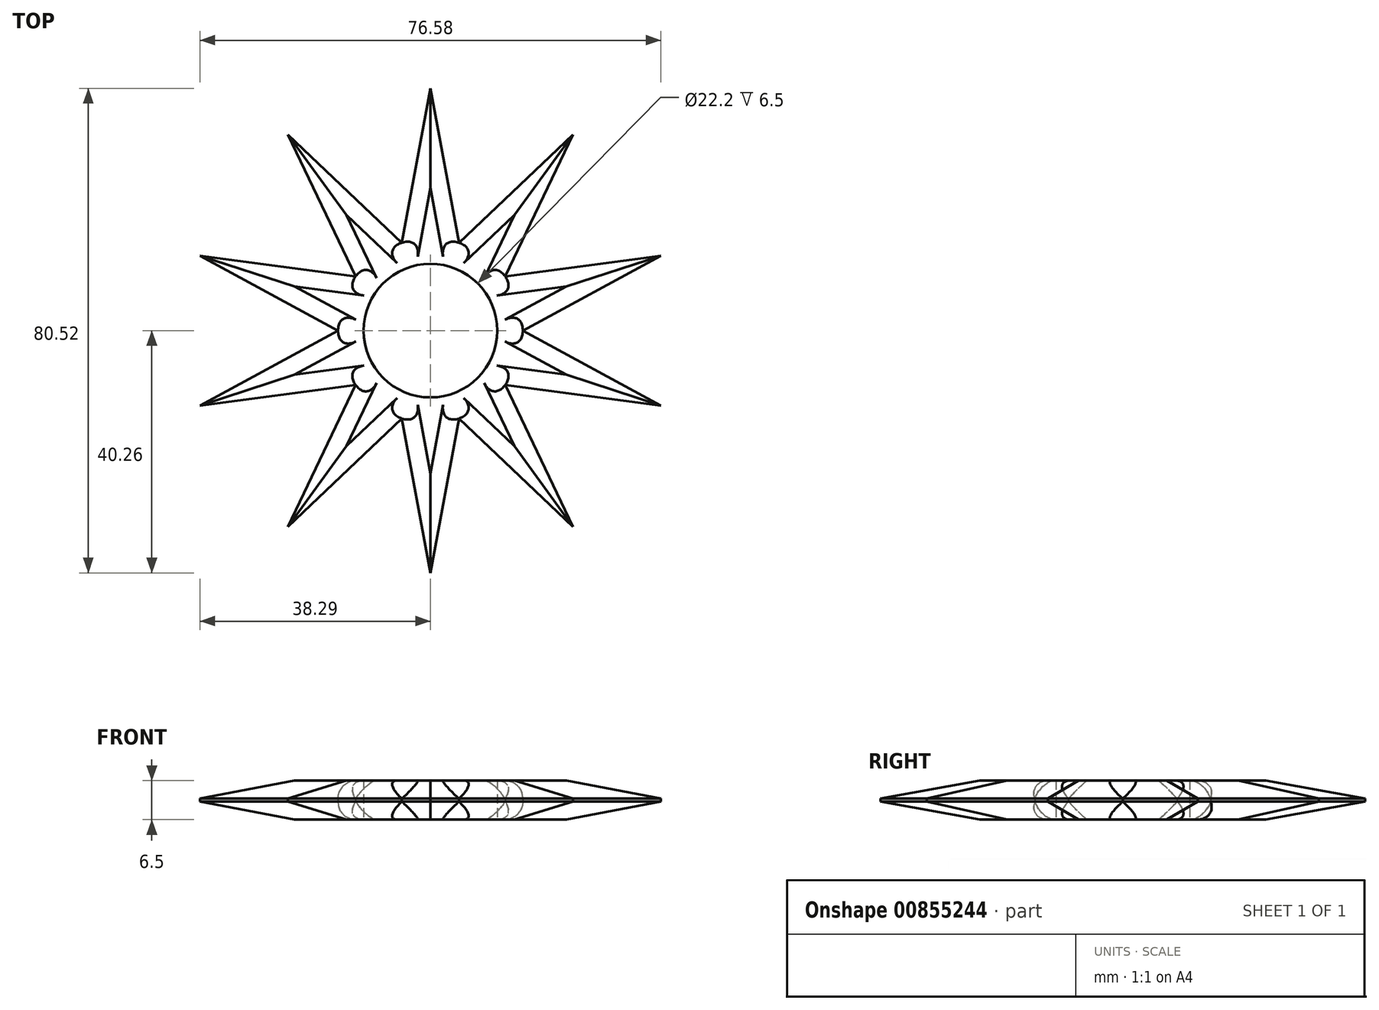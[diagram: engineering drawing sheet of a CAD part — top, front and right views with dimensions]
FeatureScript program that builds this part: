
annotation { "Feature Type Name" : "Feature", "Feature Type Description" : "" }
export const myFeature = defineFeature(function(context is Context, id is Id, definition is map)
    precondition{}
    {
        {
            var Q0;
            Q0=qCreatedBy(makeId("Top.planeOp"),FACE);
            var sketch = newSketch(context, id + "F0", { "sketchPlane" : qUnion([Q0])});
            skCircle(sketch, "E0", {"center": v(0, 0) * mm, "radius": 11.1 * mm});
            skArc(sketch, "E1", {"start": v(-4.74, 14.62) * mm, "mid": v(-4.75, 14.61) * mm, "end": v(-4.76, 14.61) * mm});
            skLineSegment(sketch, "E2", {"start": v(-4.74, 14.62) * mm, "end": v(0, 40.26) * mm});
            skLineSegment(sketch, "E3", {"start": v(0, 40.26) * mm, "end": v(4.74, 14.62) * mm});
            skLineSegment(sketch, "E4.1.0", {"start": v(-23.66, 32.57) * mm, "end": v(-4.76, 14.61) * mm});
            skLineSegment(sketch, "E4.1.1", {"start": v(-12.43, 9.04) * mm, "end": v(-23.66, 32.57) * mm});
            skLineSegment(sketch, "E4.2.0", {"start": v(-38.29, 12.44) * mm, "end": v(-12.43, 9.02) * mm});
            skLineSegment(sketch, "E4.2.1", {"start": v(-15.36, 0) * mm, "end": v(-38.29, 12.44) * mm});
            skLineSegment(sketch, "E4.3.0", {"start": v(-38.29, -12.44) * mm, "end": v(-15.36, 0) * mm});
            skLineSegment(sketch, "E4.3.1", {"start": v(-12.43, -9.02) * mm, "end": v(-38.29, -12.44) * mm});
            skLineSegment(sketch, "E4.4.0", {"start": v(-23.66, -32.57) * mm, "end": v(-12.43, -9.04) * mm});
            skLineSegment(sketch, "E4.4.1", {"start": v(-4.76, -14.61) * mm, "end": v(-23.66, -32.57) * mm});
            skLineSegment(sketch, "E4.5.0", {"start": v(0, -40.26) * mm, "end": v(-4.74, -14.62) * mm});
            skLineSegment(sketch, "E4.5.1", {"start": v(4.74, -14.62) * mm, "end": v(0, -40.26) * mm});
            skLineSegment(sketch, "E4.6.0", {"start": v(23.66, -32.57) * mm, "end": v(4.76, -14.61) * mm});
            skLineSegment(sketch, "E4.6.1", {"start": v(12.43, -9.04) * mm, "end": v(23.66, -32.57) * mm});
            skLineSegment(sketch, "E4.7.0", {"start": v(38.29, -12.44) * mm, "end": v(12.43, -9.02) * mm});
            skLineSegment(sketch, "E4.7.1", {"start": v(15.36, 0) * mm, "end": v(38.29, -12.44) * mm});
            skLineSegment(sketch, "E4.8.0", {"start": v(38.29, 12.44) * mm, "end": v(15.36, 0) * mm});
            skLineSegment(sketch, "E4.8.1", {"start": v(12.43, 9.02) * mm, "end": v(38.29, 12.44) * mm});
            skLineSegment(sketch, "E4.9.0", {"start": v(23.66, 32.57) * mm, "end": v(12.43, 9.04) * mm});
            skLineSegment(sketch, "E4.9.1", {"start": v(4.76, 14.61) * mm, "end": v(23.66, 32.57) * mm});
            skArc(sketch, "E5.trimOffspring", {"start": v(4.76, 14.61) * mm, "mid": v(4.75, 14.61) * mm, "end": v(4.74, 14.62) * mm});
            skArc(sketch, "E6.trimOffspring", {"start": v(12.43, 9.02) * mm, "mid": v(12.43, 9.03) * mm, "end": v(12.43, 9.04) * mm});
            skArc(sketch, "E7.trimOffspring", {"start": v(15.36, 0) * mm, "mid": v(15.36, 0) * mm, "end": v(15.36, 0) * mm});
            skArc(sketch, "E8.trimOffspring", {"start": v(12.43, -9.04) * mm, "mid": v(12.43, -9.03) * mm, "end": v(12.43, -9.02) * mm});
            skArc(sketch, "E9.trimOffspring", {"start": v(4.74, -14.62) * mm, "mid": v(4.75, -14.61) * mm, "end": v(4.76, -14.61) * mm});
            skArc(sketch, "E10.trimOffspring", {"start": v(-4.76, -14.61) * mm, "mid": v(-4.75, -14.61) * mm, "end": v(-4.74, -14.62) * mm});
            skArc(sketch, "E11.trimOffspring", {"start": v(-12.43, -9.02) * mm, "mid": v(-12.43, -9.03) * mm, "end": v(-12.43, -9.04) * mm});
            skArc(sketch, "E12.trimOffspring", {"start": v(-15.36, 0) * mm, "mid": v(-15.36, 0) * mm, "end": v(-15.36, 0) * mm});
            skArc(sketch, "E13.trimOffspring", {"start": v(-12.43, 9.04) * mm, "mid": v(-12.43, 9.03) * mm, "end": v(-12.43, 9.02) * mm});
            skSolve(sketch);
        }
        {
            var Q0;
            Q0=makeQuery(id+"F0.imprint","IMPRINT",FACE,{"disambiguationData":[TD([[makeQuery(id+"F0.imprint","IMPRINT",EDGE,{"derivedFrom":sQuery(id+"F0.wireOp",EDGE,"E0")}),-1.0]])]});
            extrude(context, id + "F1", {"entities" : qUnion([Q0]), "depth" : 6.5 * mm, "offsetDistance" : 25 * mm});
        }
        {
            var Q0;
            Q0=makeQuery(id+"F1.opExtrude","CAP_EDGE",EDGE,{"disambiguationData":[OSD([sQuery(id+"F0.wireOp",EDGE,"E4.3.0")])],"isStart":false});
            var Q1;
            Q1=makeQuery(id+"F1.opExtrude","CAP_EDGE",EDGE,{"disambiguationData":[OSD([sQuery(id+"F0.wireOp",EDGE,"E4.2.1")])],"isStart":false});
            var Q2;
            Q2=makeQuery(id+"F1.opExtrude","CAP_EDGE",EDGE,{"disambiguationData":[OSD([sQuery(id+"F0.wireOp",EDGE,"E4.2.0")])],"isStart":false});
            var Q3;
            Q3=makeQuery(id+"F1.opExtrude","CAP_EDGE",EDGE,{"disambiguationData":[OSD([sQuery(id+"F0.wireOp",EDGE,"E4.1.1")])],"isStart":false});
            var Q4;
            Q4=makeQuery(id+"F1.opExtrude","CAP_EDGE",EDGE,{"disambiguationData":[OSD([sQuery(id+"F0.wireOp",EDGE,"E4.1.0")])],"isStart":false});
            var Q5;
            Q5=makeQuery(id+"F1.opExtrude","CAP_EDGE",EDGE,{"disambiguationData":[OSD([sQuery(id+"F0.wireOp",EDGE,"E2")])],"isStart":false});
            var Q6;
            Q6=makeQuery(id+"F1.opExtrude","CAP_EDGE",EDGE,{"disambiguationData":[OSD([sQuery(id+"F0.wireOp",EDGE,"E3")])],"isStart":false});
            var Q7;
            Q7=makeQuery(id+"F1.opExtrude","CAP_EDGE",EDGE,{"disambiguationData":[OSD([sQuery(id+"F0.wireOp",EDGE,"E4.9.1")])],"isStart":false});
            var Q8;
            Q8=makeQuery(id+"F1.opExtrude","CAP_EDGE",EDGE,{"disambiguationData":[OSD([sQuery(id+"F0.wireOp",EDGE,"E4.9.0")])],"isStart":false});
            var Q9;
            Q9=makeQuery(id+"F1.opExtrude","CAP_EDGE",EDGE,{"disambiguationData":[OSD([sQuery(id+"F0.wireOp",EDGE,"E4.8.1")])],"isStart":false});
            var Q10;
            Q10=makeQuery(id+"F1.opExtrude","CAP_EDGE",EDGE,{"disambiguationData":[OSD([sQuery(id+"F0.wireOp",EDGE,"E4.8.0")])],"isStart":false});
            var Q11;
            Q11=makeQuery(id+"F1.opExtrude","CAP_EDGE",EDGE,{"disambiguationData":[OSD([sQuery(id+"F0.wireOp",EDGE,"E4.7.1")])],"isStart":false});
            var Q12;
            Q12=makeQuery(id+"F1.opExtrude","CAP_EDGE",EDGE,{"disambiguationData":[OSD([sQuery(id+"F0.wireOp",EDGE,"E4.7.0")])],"isStart":false});
            var Q13;
            Q13=makeQuery(id+"F1.opExtrude","CAP_EDGE",EDGE,{"disambiguationData":[OSD([sQuery(id+"F0.wireOp",EDGE,"E4.6.1")])],"isStart":false});
            var Q14;
            Q14=makeQuery(id+"F1.opExtrude","CAP_EDGE",EDGE,{"disambiguationData":[OSD([sQuery(id+"F0.wireOp",EDGE,"E4.6.0")])],"isStart":false});
            var Q15;
            Q15=makeQuery(id+"F1.opExtrude","CAP_EDGE",EDGE,{"disambiguationData":[OSD([sQuery(id+"F0.wireOp",EDGE,"E4.5.1")])],"isStart":false});
            var Q16;
            Q16=makeQuery(id+"F1.opExtrude","CAP_EDGE",EDGE,{"disambiguationData":[OSD([sQuery(id+"F0.wireOp",EDGE,"E4.4.0")])],"isStart":false});
            var Q17;
            Q17=makeQuery(id+"F1.opExtrude","CAP_EDGE",EDGE,{"disambiguationData":[OSD([sQuery(id+"F0.wireOp",EDGE,"E4.2.1")])],"isStart":true});
            var Q18;
            Q18=makeQuery(id+"F1.opExtrude","CAP_EDGE",EDGE,{"disambiguationData":[OSD([sQuery(id+"F0.wireOp",EDGE,"E4.2.0")])],"isStart":true});
            var Q19;
            Q19=makeQuery(id+"F1.opExtrude","CAP_EDGE",EDGE,{"disambiguationData":[OSD([sQuery(id+"F0.wireOp",EDGE,"E4.3.0")])],"isStart":true});
            var Q20;
            Q20=makeQuery(id+"F1.opExtrude","CAP_EDGE",EDGE,{"disambiguationData":[OSD([sQuery(id+"F0.wireOp",EDGE,"E4.3.1")])],"isStart":true});
            var Q21;
            Q21=makeQuery(id+"F1.opExtrude","CAP_EDGE",EDGE,{"disambiguationData":[OSD([sQuery(id+"F0.wireOp",EDGE,"E4.4.1")])],"isStart":true});
            var Q22;
            Q22=makeQuery(id+"F1.opExtrude","CAP_EDGE",EDGE,{"disambiguationData":[OSD([sQuery(id+"F0.wireOp",EDGE,"E4.4.0")])],"isStart":true});
            var Q23;
            Q23=makeQuery(id+"F1.opExtrude","CAP_EDGE",EDGE,{"disambiguationData":[OSD([sQuery(id+"F0.wireOp",EDGE,"E4.5.0")])],"isStart":true});
            var Q24;
            Q24=makeQuery(id+"F1.opExtrude","CAP_EDGE",EDGE,{"disambiguationData":[OSD([sQuery(id+"F0.wireOp",EDGE,"E4.5.1")])],"isStart":true});
            var Q25;
            Q25=makeQuery(id+"F1.opExtrude","CAP_EDGE",EDGE,{"disambiguationData":[OSD([sQuery(id+"F0.wireOp",EDGE,"E4.6.0")])],"isStart":true});
            var Q26;
            Q26=makeQuery(id+"F1.opExtrude","CAP_EDGE",EDGE,{"disambiguationData":[OSD([sQuery(id+"F0.wireOp",EDGE,"E4.6.1")])],"isStart":true});
            var Q27;
            Q27=makeQuery(id+"F1.opExtrude","CAP_EDGE",EDGE,{"disambiguationData":[OSD([sQuery(id+"F0.wireOp",EDGE,"E4.7.0")])],"isStart":true});
            var Q28;
            Q28=makeQuery(id+"F1.opExtrude","CAP_EDGE",EDGE,{"disambiguationData":[OSD([sQuery(id+"F0.wireOp",EDGE,"E4.7.1")])],"isStart":true});
            var Q29;
            Q29=makeQuery(id+"F1.opExtrude","CAP_EDGE",EDGE,{"disambiguationData":[OSD([sQuery(id+"F0.wireOp",EDGE,"E4.8.0")])],"isStart":true});
            var Q30;
            Q30=makeQuery(id+"F1.opExtrude","CAP_EDGE",EDGE,{"disambiguationData":[OSD([sQuery(id+"F0.wireOp",EDGE,"E4.8.1")])],"isStart":true});
            var Q31;
            Q31=makeQuery(id+"F1.opExtrude","CAP_EDGE",EDGE,{"disambiguationData":[OSD([sQuery(id+"F0.wireOp",EDGE,"E4.9.0")])],"isStart":true});
            var Q32;
            Q32=makeQuery(id+"F1.opExtrude","CAP_EDGE",EDGE,{"disambiguationData":[OSD([sQuery(id+"F0.wireOp",EDGE,"E4.9.1")])],"isStart":true});
            var Q33;
            Q33=makeQuery(id+"F1.opExtrude","CAP_EDGE",EDGE,{"disambiguationData":[OSD([sQuery(id+"F0.wireOp",EDGE,"E3")])],"isStart":true});
            var Q34;
            Q34=makeQuery(id+"F1.opExtrude","CAP_EDGE",EDGE,{"disambiguationData":[OSD([sQuery(id+"F0.wireOp",EDGE,"E2")])],"isStart":true});
            var Q35;
            Q35=makeQuery(id+"F1.opExtrude","CAP_EDGE",EDGE,{"disambiguationData":[OSD([sQuery(id+"F0.wireOp",EDGE,"E4.1.0")])],"isStart":true});
            var Q36;
            Q36=makeQuery(id+"F1.opExtrude","CAP_EDGE",EDGE,{"disambiguationData":[OSD([sQuery(id+"F0.wireOp",EDGE,"E4.1.1")])],"isStart":true});
            var Q37;
            Q37=makeQuery(id+"F1.opExtrude","CAP_EDGE",EDGE,{"disambiguationData":[OSD([sQuery(id+"F0.wireOp",EDGE,"E4.3.1")])],"isStart":false});
            var Q38;
            Q38=makeQuery(id+"F1.opExtrude","CAP_EDGE",EDGE,{"disambiguationData":[OSD([sQuery(id+"F0.wireOp",EDGE,"E4.4.1")])],"isStart":false});
            var Q39;
            Q39=makeQuery(id+"F1.opExtrude","CAP_EDGE",EDGE,{"disambiguationData":[OSD([sQuery(id+"F0.wireOp",EDGE,"E4.5.0")])],"isStart":false});
            chamfer(context, id + "F2", {"entities" : qUnion([Q0, Q1, Q2, Q3, Q4, Q5, Q6, Q7, Q8, Q9, Q10, Q11, Q12, Q13, Q14, Q15, Q16, Q17, Q18, Q19, Q20, Q21, Q22, Q23, Q24, Q25, Q26, Q27, Q28, Q29, Q30, Q31, Q32, Q33, Q34, Q35, Q36, Q37, Q38, Q39]), "width" : 3 * mm, "tangentPropagation" : true});
        }
        {
            var Q0;
            Q0=makeQuery(id+"F1.opExtrude","CAP_EDGE",EDGE,{"disambiguationData":[OSD([sQuery(id+"F0.wireOp",EDGE,"E12.trimOffspring")])],"isStart":true});
            var Q1;
            Q1=makeQuery(id+"F1.opExtrude","CAP_EDGE",EDGE,{"disambiguationData":[OSD([sQuery(id+"F0.wireOp",EDGE,"E11.trimOffspring")])],"isStart":true});
            var Q2;
            Q2=makeQuery(id+"F1.opExtrude","CAP_EDGE",EDGE,{"disambiguationData":[OSD([sQuery(id+"F0.wireOp",EDGE,"E10.trimOffspring")])],"isStart":true});
            var Q3;
            Q3=makeQuery(id+"F1.opExtrude","CAP_EDGE",EDGE,{"disambiguationData":[OSD([sQuery(id+"F0.wireOp",EDGE,"E9.trimOffspring")])],"isStart":true});
            var Q4;
            Q4=makeQuery(id+"F1.opExtrude","CAP_EDGE",EDGE,{"disambiguationData":[OSD([sQuery(id+"F0.wireOp",EDGE,"E8.trimOffspring")])],"isStart":true});
            var Q5;
            Q5=makeQuery(id+"F1.opExtrude","CAP_EDGE",EDGE,{"disambiguationData":[OSD([sQuery(id+"F0.wireOp",EDGE,"E7.trimOffspring")])],"isStart":true});
            var Q6;
            Q6=makeQuery(id+"F1.opExtrude","CAP_EDGE",EDGE,{"disambiguationData":[OSD([sQuery(id+"F0.wireOp",EDGE,"E6.trimOffspring")])],"isStart":true});
            var Q7;
            Q7=makeQuery(id+"F1.opExtrude","CAP_EDGE",EDGE,{"disambiguationData":[OSD([sQuery(id+"F0.wireOp",EDGE,"E5.trimOffspring")])],"isStart":true});
            var Q8;
            Q8=makeQuery(id+"F1.opExtrude","CAP_EDGE",EDGE,{"disambiguationData":[OSD([sQuery(id+"F0.wireOp",EDGE,"E1")])],"isStart":true});
            var Q9;
            Q9=makeQuery(id+"F1.opExtrude","CAP_EDGE",EDGE,{"disambiguationData":[OSD([sQuery(id+"F0.wireOp",EDGE,"E13.trimOffspring")])],"isStart":true});
            var Q10;
            Q10=makeQuery(id+"F1.opExtrude","CAP_EDGE",EDGE,{"disambiguationData":[OSD([sQuery(id+"F0.wireOp",EDGE,"E6.trimOffspring")])],"isStart":false});
            var Q11;
            Q11=makeQuery(id+"F1.opExtrude","CAP_EDGE",EDGE,{"disambiguationData":[OSD([sQuery(id+"F0.wireOp",EDGE,"E5.trimOffspring")])],"isStart":false});
            var Q12;
            Q12=makeQuery(id+"F1.opExtrude","CAP_EDGE",EDGE,{"disambiguationData":[OSD([sQuery(id+"F0.wireOp",EDGE,"E1")])],"isStart":false});
            var Q13;
            Q13=makeQuery(id+"F1.opExtrude","CAP_EDGE",EDGE,{"disambiguationData":[OSD([sQuery(id+"F0.wireOp",EDGE,"E13.trimOffspring")])],"isStart":false});
            var Q14;
            Q14=makeQuery(id+"F1.opExtrude","CAP_EDGE",EDGE,{"disambiguationData":[OSD([sQuery(id+"F0.wireOp",EDGE,"E12.trimOffspring")])],"isStart":false});
            var Q15;
            Q15=makeQuery(id+"F1.opExtrude","CAP_EDGE",EDGE,{"disambiguationData":[OSD([sQuery(id+"F0.wireOp",EDGE,"E11.trimOffspring")])],"isStart":false});
            var Q16;
            Q16=makeQuery(id+"F1.opExtrude","CAP_EDGE",EDGE,{"disambiguationData":[OSD([sQuery(id+"F0.wireOp",EDGE,"E10.trimOffspring")])],"isStart":false});
            var Q17;
            Q17=makeQuery(id+"F1.opExtrude","CAP_EDGE",EDGE,{"disambiguationData":[OSD([sQuery(id+"F0.wireOp",EDGE,"E9.trimOffspring")])],"isStart":false});
            var Q18;
            Q18=makeQuery(id+"F1.opExtrude","CAP_EDGE",EDGE,{"disambiguationData":[OSD([sQuery(id+"F0.wireOp",EDGE,"E8.trimOffspring")])],"isStart":false});
            var Q19;
            Q19=makeQuery(id+"F1.opExtrude","CAP_EDGE",EDGE,{"disambiguationData":[OSD([sQuery(id+"F0.wireOp",EDGE,"E7.trimOffspring")])],"isStart":false});
            fillet(context, id + "F3", {"entities" : qUnion([Q0, Q1, Q2, Q3, Q4, Q5, Q6, Q7, Q8, Q9, Q10, Q11, Q12, Q13, Q14, Q15, Q16, Q17, Q18, Q19]), "radius" : 3 * mm, "tangentPropagation" : true, "allowEdgeOverflow" : false});
        }
    });
